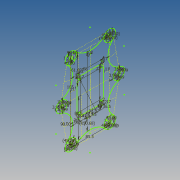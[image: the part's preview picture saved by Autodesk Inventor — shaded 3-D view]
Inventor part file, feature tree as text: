
AUTODESK INVENTOR PART (.ipt)
format: ipt  version: 2014 (Build 180170000, 170)  size: 195,072 bytes
history: native  units: mm
features: sketch x4
ambient origin geometry x8: Origin, YZ Plane, XZ Plane, XY Plane, X Axis, Y Axis, Z Axis, Center Point
feature tree (4):
  sketch  "Sketch1"  dims[d0=165.0mm d1=85.5mm d2=82.5mm d3=20.0mm d4=20.0mm d5=25.0mm d6=25.0mm d7=25.0mm d8=25.0mm d9=25.0mm d10=25.0mm d11=7.0mm d12=7.0mm d13=7.0mm d14=7.0mm d15=7.0mm d16=7.0mm d17=45.0deg d18=45.0deg d19=45.0deg d20=45.0deg d21=45.0deg d22=45.0deg d23=45.0deg d24=90.0deg d27=11.0mm d28=11.0mm d29=150.680282mm d30=61.6967mm d43=2.0mm d44=6.5mm d45=2.0mm d46=2.0mm d48=17.0mm d49=17.0mm d51=2.0mm d52=2.0mm d55=17.0mm d56=17.0mm]
  sketch  "Sketch2"  dims[d57=2.0mm]
  sketch  "Sketch3"  dims[d58=2.0mm]
  sketch  "Sketch4"  dims[d59=8.0mm d60=8.0mm d61=2.0mm d62=8.0mm d63=2.0mm d64=8.0mm d66=60.0mm d67=42.0mm d68=60.0mm d69=42.0mm d70=58.0mm d71=76.0mm d72=2.0mm d73=5.5mm d74=5.5mm d75=12.5mm d76=12.5mm d77=36.5mm d78=36.5mm d79=90.0deg d80=90.0deg d81=90.0deg d82=90.0deg d83=90.0deg d88=1.5mm d89=1.5mm d90=1.5mm d91=1.5mm d92=1.5mm d93=1.5mm d94=1.5mm d95=1.5mm d96=3.999mm d97=3.999mm d98=3.999mm d99=3.999mm d100=1.5mm d101=1.5mm d102=1.5mm d103=1.5mm d104=3.998972mm d105=3.998972mm d106=3.999mm d107=3.999mm d109=1.5mm d110=1.5mm d111=1.5mm d112=1.5mm d113=3.999mm d114=1.5mm d115=1.5mm d116=1.5mm d117=1.5mm d118=3.999mm d119=1.5mm d120=1.5mm d121=1.5mm d122=1.5mm]
